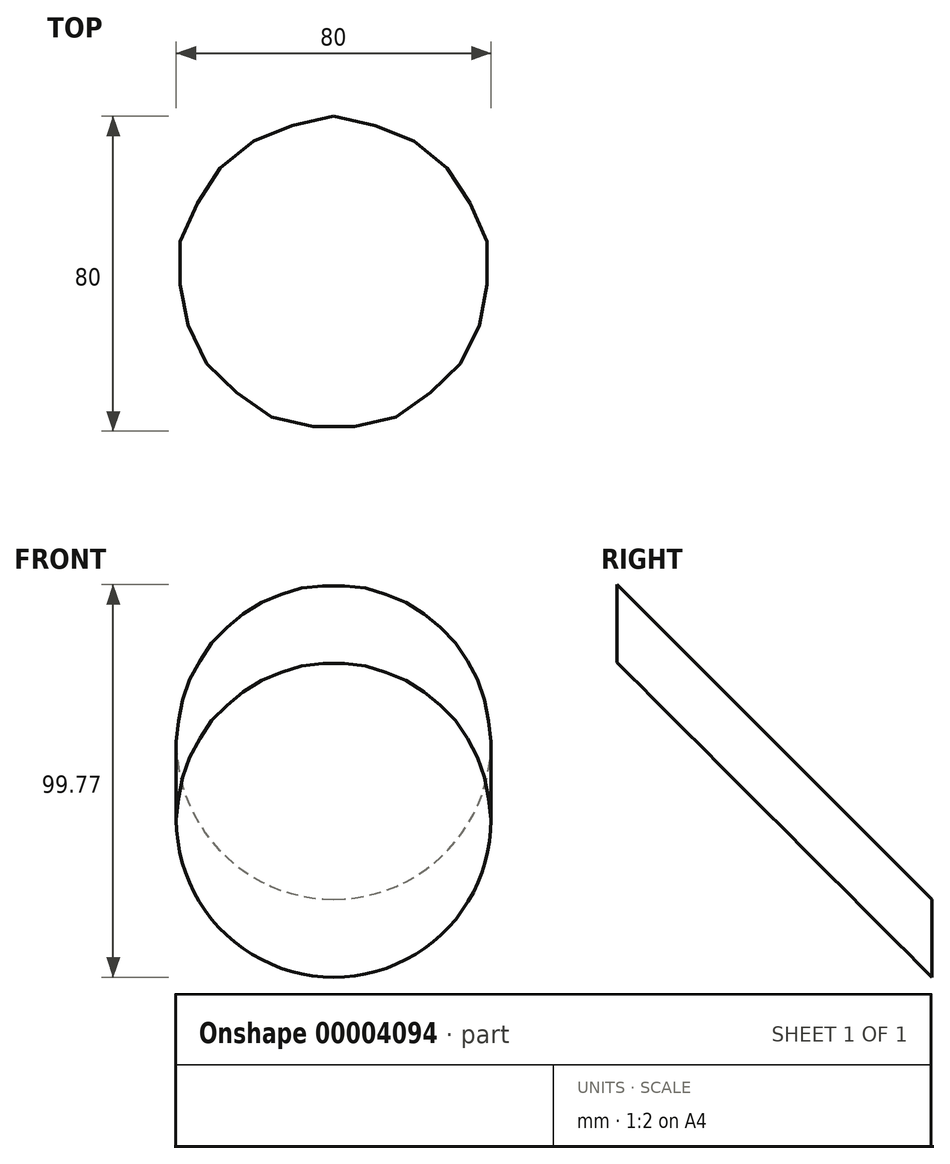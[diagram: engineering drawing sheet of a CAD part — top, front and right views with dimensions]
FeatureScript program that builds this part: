
annotation { "Feature Type Name" : "Feature", "Feature Type Description" : "" }
export const myFeature = defineFeature(function(context is Context, id is Id, definition is map)
    precondition{}
    {
        {
            var Q0;
            Q0=qCreatedBy(makeId("Top.planeOp"),FACE);
            var sketch = newSketch(context, id + "F0", { "sketchPlane" : qUnion([Q0]), "disableImprinting" : false});
            skCircle(sketch, "E0", {"center": v(0, 0) * mm, "radius": 40 * mm});
            skSolve(sketch);
        }
        {
            var Q0;
            Q0=makeQuery(id+"F0.imprint","IMPRINT",FACE,{"disambiguationData":[TD([[makeQuery(id+"F0.imprint","IMPRINT",EDGE,{"derivedFrom":sQuery(id+"F0.wireOp",EDGE,"E0")}),1.0]])]});
            extrude(context, id + "F1", {"entities" : qUnion([Q0]), "depth" : 100 * mm});
        }
        {
            var Q0;
            Q0=qCreatedBy(makeId("Right.planeOp"),FACE);
            var sketch = newSketch(context, id + "F2", { "sketchPlane" : qUnion([Q0])});
            skLineSegment(sketch, "E1.0", {"start": v(-40, 0) * mm, "end": v(40, 0) * mm});
            skLineSegment(sketch, "E2", {"start": v(40, 0) * mm, "end": v(-41.81, 81.81) * mm});
            skLineSegment(sketch, "E3", {"start": v(-42.18, 101.95) * mm, "end": v(40.49, 19.28) * mm});
            skLineSegment(sketch, "E4", {"start": v(-41.81, 81.81) * mm, "end": v(-40, 0) * mm});
            skLineSegment(sketch, "E5", {"start": v(40.49, 19.28) * mm, "end": v(42, 104.27) * mm});
            skLineSegment(sketch, "E6", {"start": v(42, 104.27) * mm, "end": v(-43.61, 101.95) * mm});
            skLineSegment(sketch, "E7", {"start": v(-43.61, 101.95) * mm, "end": v(-42.18, 101.95) * mm});
            skSolve(sketch);
        }
        {
            var Q0;
            {Q0=qUnion([makeQuery(id+"F2.imprint","IMPRINT",FACE,{"disambiguationData":[TD([[makeQuery(id+"F2.imprint","IMPRINT",EDGE,{"derivedFrom":sQuery(id+"F2.wireOp",EDGE,"E1.0")}),1.0]])]}),makeQuery(id+"F2.imprint","IMPRINT",FACE,{"disambiguationData":[TD([[makeQuery(id+"F2.imprint","IMPRINT",EDGE,{"derivedFrom":sQuery(id+"F2.wireOp",EDGE,"E3")}),1.0]])]})]);}
            extrude(context, id + "F3", {"entities" : qUnion([Q0]), "operationType" : NewBodyOperationType.REMOVE, "oppositeDirection" : true, "depth" : 100 * mm, "symmetric" : true});
        }
    });
